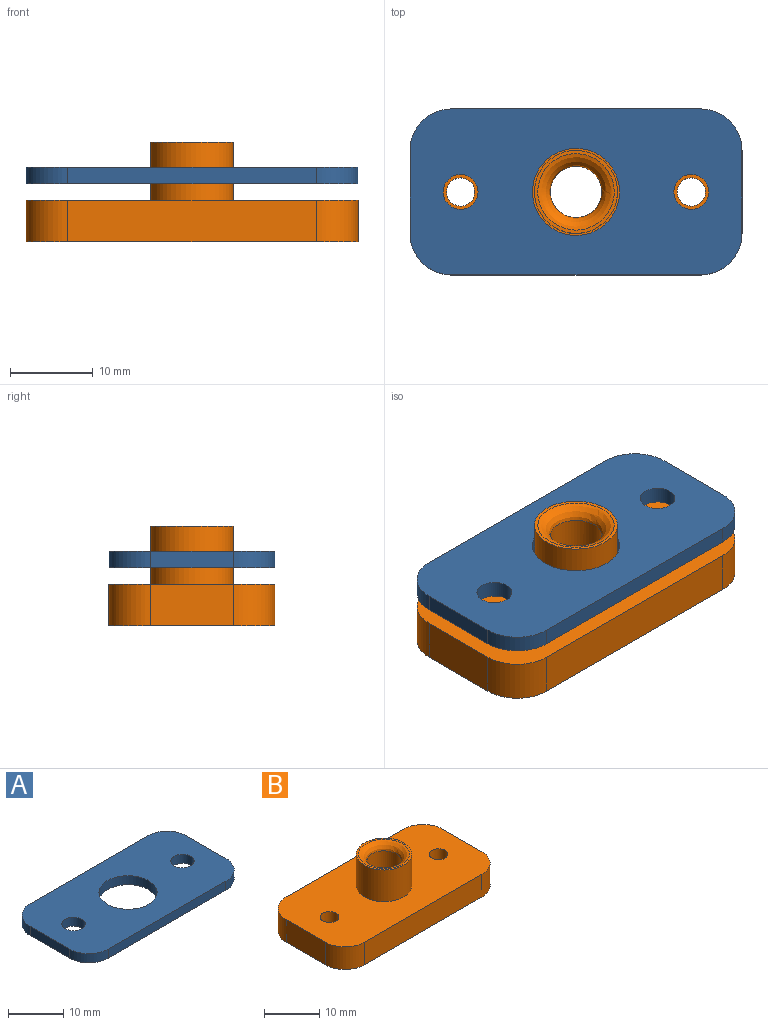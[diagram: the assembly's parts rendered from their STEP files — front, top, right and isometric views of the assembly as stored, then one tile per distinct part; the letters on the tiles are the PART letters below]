
ASSEMBLY  parts=2 mates=1
PART A: 13 faces, bbox 40x20x2 mm
  f0: plane 10x2mm, normal (1,0,0), area 20mm2, adj f1,f10,f11,f12
  f1: cylinder r=5mm len=5mm, axis (0,0,-1), area 15.7mm2, adj f0,f2,f11,f12
  f2: plane 30x2mm, normal (0,1,0), area 60mm2, adj f1,f3,f11,f12
  f3: cylinder r=5mm len=5mm, axis (0,0,-1), area 15.7mm2, adj f2,f4,f11,f12
  f4: plane 10x2mm, normal (-1,0,0), area 20mm2, adj f3,f5,f11,f12
  f5: cylinder r=5mm len=5mm, axis (0,0,-1), area 15.7mm2, adj f4,f6,f11,f12
  f6: plane 30x2mm, normal (0,-1,0), area 60mm2, adj f5,f10,f11,f12
  f7: cylinder r=5.25mm len=10.5mm, axis (0,0,-1), area 66mm2, adj f11,f12
  f8: cylinder r=2.1mm len=4.2mm, axis (0,0,-1), area 26.4mm2, adj f11,f12
  f9: cylinder r=2.1mm len=4.2mm, axis (0,0,-1), area 26.4mm2, adj f11,f12
  f10: cylinder r=5mm len=5mm, axis (0,0,-1), area 15.7mm2, adj f0,f6,f11,f12
  f11: plane 40x20mm, normal (0,0,1), area 664.2mm2, adj f0,f1,f2,f3,f4,f5,f6,f7
  f12: plane 40x20mm, normal (0,0,-1), area 664.2mm2, adj f0,f1,f2,f3,f4,f5,f6,f7
PART B: 16 faces, bbox 40x20x12 mm
  f0: plane 10x5mm, normal (1,0,0), area 50mm2, adj f1,f9,f10,f11
  f1: cylinder r=5mm len=5mm, axis (0,0,-1), area 39.3mm2, adj f0,f2,f10,f11
  f2: plane 30x5mm, normal (0,1,0), area 150mm2, adj f1,f3,f10,f11
  f3: cylinder r=5mm len=5mm, axis (0,0,-1), area 39.3mm2, adj f2,f4,f10,f11
  f4: plane 10x5mm, normal (-1,0,0), area 50mm2, adj f3,f5,f10,f11
  f5: cylinder r=5mm len=5mm, axis (0,0,-1), area 39.3mm2, adj f4,f6,f10,f11
  f6: plane 30x5mm, normal (0,-1,0), area 150mm2, adj f5,f9,f10,f11
  f7: cylinder r=1.7mm len=5mm, axis (0,0,-1), area 53.4mm2, adj f10,f11
  f8: cylinder r=1.7mm len=5mm, axis (0,0,-1), area 53.4mm2, adj f10,f11
  f9: cylinder r=5mm len=5mm, axis (0,0,-1), area 39.3mm2, adj f0,f6,f10,f11
  f10: plane 40x20mm, normal (0,0,1), area 681.8mm2, adj f0,f1,f2,f3,f4,f5,f6,f7
  f11: plane 40x20mm, normal (0,0,-1), area 730.2mm2, adj f0,f1,f2,f3,f4,f5,f6,f7
  f12: cylinder r=3.1mm len=10.5mm, axis (0,0,-1), area 204.5mm2, adj f11,f13
  f13: bspline ~9.2x9.2mm, area 52.5mm2, adj f12,f15
  f14: cylinder r=5mm len=10mm, axis (0,0,-1), area 219.9mm2, adj f10,f15
  f15: plane 10.01x10.01mm, normal (0,0,1), area 12.1mm2, adj f13,f14
PLACE A t=(-16.67,7.66,4.62)mm
PLACE B t=(-16.67,7.66,-2.38)mm
MATE fastened A.f7 <-> B.f12  axis (0,0,-1) through (-16.67,7.66,4.62)mm
